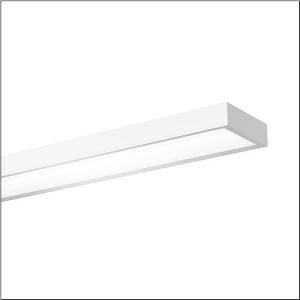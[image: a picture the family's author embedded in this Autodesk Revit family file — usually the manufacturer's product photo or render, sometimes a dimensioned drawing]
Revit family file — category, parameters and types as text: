
# Revit family: sport_31_51hs12dc3dca
name_source: partatom
category: Lighting Fixtures
units: mm (PartAtom-declared; Revit-internal decimal feet)

## family parameters
Cut with Voids When Loaded = No
Host = Face
Light Source = No
Part Type = Normal
Room Calculation Point = No
Round Connector Dimension = Use Diameter
Shared = No

## types (1)
- --- (1 x LED, 7500 lm, 55.4 W, 3000K)
    Apparent Load = 55 VA
    CIE Flux Codes = 65 89 97 100 100
    Color Rendering = 80
    Color Temperature = 3000K
    Default Elevation = 1800 mm
    Description = Sport 31, high bay luminaire, primary light control with reflector, of sheet steel, primary anti-glare with prismatic structure, of PC, primary optical cover: cover panel, of PC, light emission: direct distribution, primary light characteristic: symmetric, installation type: suspended mounting, recessed, surface-mounted, LED, rated luminous flux: 7.500lm, luminous efficacy: 130lm/W, light colour: 830, colour temperature: 3000K, control gear: DALI 2, with terminal, 5-pole, max. 2.5mm², mains connection: 220..240V, AC/DC, 50/60Hz, rated input power: 58W, housing, of sheet steel, traffic white (RAL 9016), length: 1.540mm, width: 315mm, height: 95mm, protection rating (complete): IP20, protection rating (lamp compartment, on room side): IP50, insulation class (complete): insulation class I (protective earthing), certification: CE, ENEC, UKCA, ball protection: ball impact resistant with ceiling mounting or chain suspension, impact resistance: IK08, permissible operating ambient temperature: -20..+35°C, standard: DIN 18032-3, EN 60598-2-22, packaging unit: 1 piece
    Height = 100 mm  [stored 0.328084 ft]
    Lamp = 1 x LED
    Lamp Light Flux = 7500 lm
    Lamp Power = 55.4 W
    Lamp count = 1
    Length = 1500 mm
    Luminous efficacy = 135 lm/W
    Manufacturer = Siteco
    ModVariant = No
    Model = 51HS12DC3DCA
    Mounting Place = Ceiling
    Mounting Type = Pendant
    Number of Poles = 1
    OnlyDefault = Yes
    Power Factor = 1
    Product Name = Sport 31
    Product group = high bay luminaire
    ProductGroupID = 902
    Protection Class = Protection class I
    Protection Degree = IP 20
    RLX_Detail_Level = 1
    RLX_Emergency_Light_Flux = 0 lm
    RLX_Emergency_Type = 0
    RLX_Emergency_Type_DB = No
    RlxData = <blob elided: 22769 chars, md5=5baf5fa6>
    Socket = socket
    Standby Power = 0 W
    System Light Flux = 7500 lm
    System Power = 55 W
    Type Comments = factory setting: luminous flux: 100 % | dim-lin: 254 | 234 mA
    Type Image = l_1397489.jpg
    URL = http://relux.com
    VarID = @adj_198515
    Voltage = 0 V
    Weight = 0.00 kg
    Width = 315 mm

note: [stored X ft] marks values corroborated as IEEE doubles in the binary element streams (Revit-internal decimal feet)

## geometry (parser evidence)
native form markers: Blend x4, Sweep x9
no freeform markers — native parametric forms only
